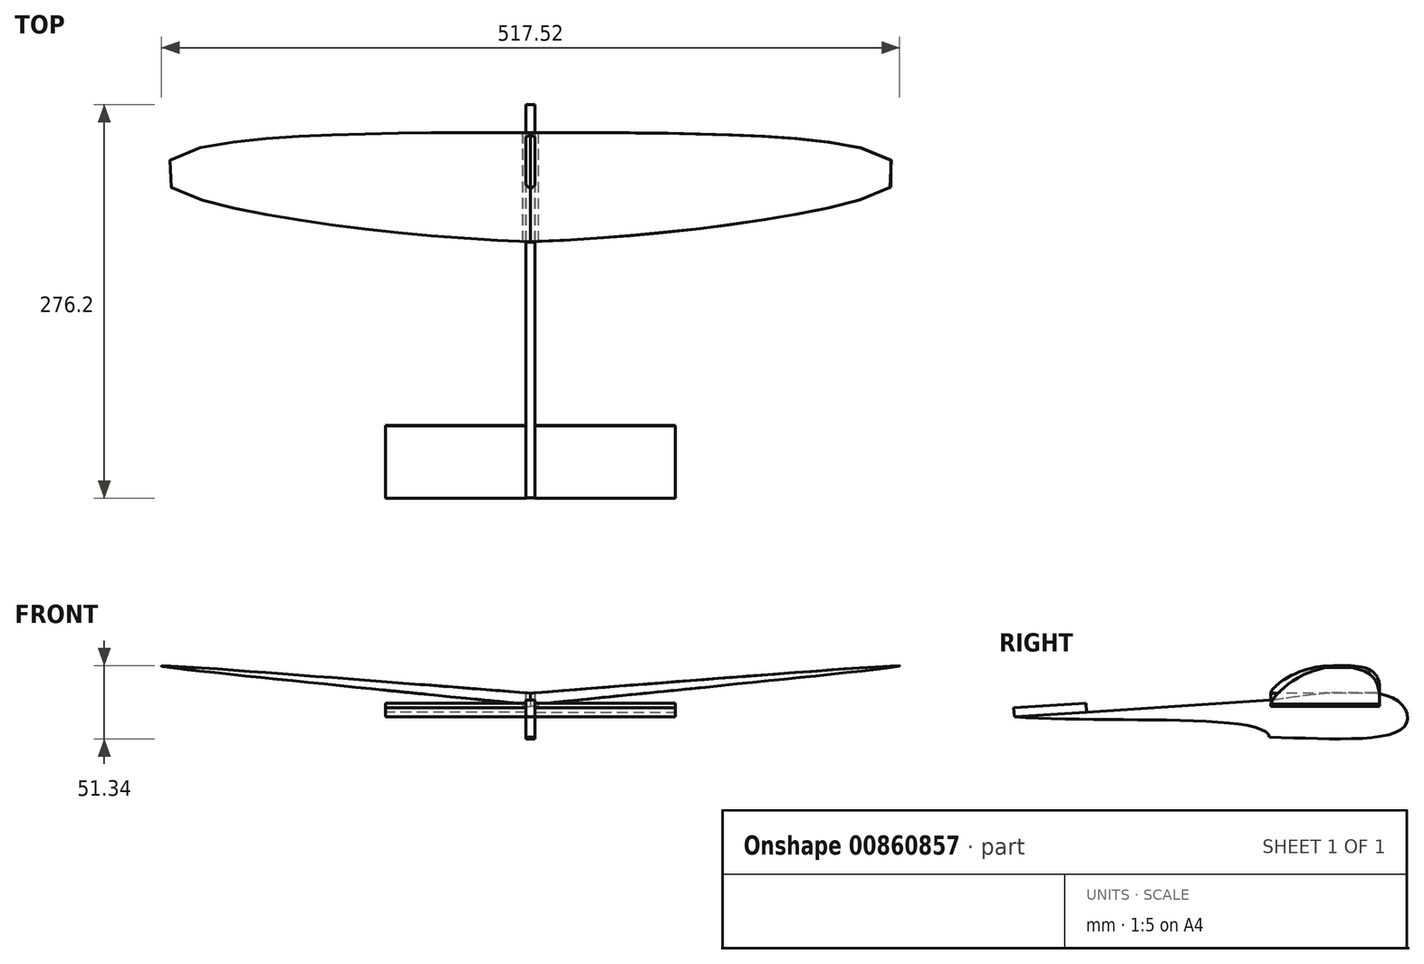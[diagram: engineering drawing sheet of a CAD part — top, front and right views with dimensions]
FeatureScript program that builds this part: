
annotation { "Feature Type Name" : "Feature", "Feature Type Description" : "" }
export const myFeature = defineFeature(function(context is Context, id is Id, definition is map)
    precondition{}
    {
        {
            var Q0;
            Q0=qCreatedBy(makeId("Top.planeOp"),FACE);
            cPlane(context, id + "F0", {"entities" : qUnion([Q0]), "cplaneType" : CPlaneType.OFFSET, "offset" : 21.59 * mm, "width" : 152.4 * mm, "height" : 152.4 * mm});
        }
        {
            var Q0;
            Q0=qCreatedBy(id+"F0.planeOp",FACE);
            var sketch = newSketch(context, id + "F1", { "sketchPlane" : qUnion([Q0])});
            skFitSpline(sketch, "E0", {"points": [v(0, 53.44) * mm, v(187.04, 49.14) * mm, v(254.61, 32.56) * mm, v(254, 16.59) * mm, v(0, -22.96) * mm], "startDerivative": vector(621.7, 0.16) * mm, "endDerivative": vector(-509.24, -9.47) * mm});
            skLineSegment(sketch, "E1", {"start": v(0, 0) * mm, "end": v(0, -100.13) * mm, "construction": true});
            skFitSpline(sketch, "E2.MirrorCS", {"points": [v(0, 53.44) * mm, v(-187.04, 49.14) * mm, v(-254.61, 32.56) * mm, v(-254, 16.59) * mm, v(0, -22.96) * mm], "startDerivative": vector(-621.7, 0.16) * mm, "endDerivative": vector(509.24, -9.47) * mm});
            skSolve(sketch);
        }
        {
            var Q0;
            Q0 = qSketchRegion(id + "F1", true);
            extrude(context, id + "F2", {"entities" : qUnion([Q0]), "depth" : 65.8 * mm, "offsetDistance" : 25.4 * mm});
        }
        {
            var Q0;
            Q0=qCreatedBy(makeId("Right.planeOp"),FACE);
            var sketch = newSketch(context, id + "F3", { "sketchPlane" : qUnion([Q0])});
            skLineSegment(sketch, "E3", {"start": v(-23.46, 26.13) * mm, "end": v(-23.7, 0) * mm});
            skLineSegment(sketch, "E4", {"start": v(-23.46, 26.13) * mm, "end": v(-202.7, 14.43) * mm});
            skFitSpline(sketch, "E5", {"points": [v(-202.7, 14.43) * mm, v(-23.7, 0) * mm], "startDerivative": vector(179.6, -14.43) * mm, "endDerivative": vector(3, -52.87) * mm});
            skFitSpline(sketch, "E6", {"points": [v(-23.46, 26.13) * mm, v(65.57, 26.13) * mm, v(70.56, 7.26) * mm, v(-23.7, 0) * mm], "startDerivative": vector(256.87, 37.76) * mm, "endDerivative": vector(-273.68, 3.75) * mm});
            skSolve(sketch);
        }
        {
            var Q0;
            Q0 = qSketchRegion(id + "F3", true);
            extrude(context, id + "F4", {"entities" : qUnion([Q0]), "endBound" : BoundingType.SYMMETRIC, "depth" : 6.35 * mm, "offsetDistance" : 25.4 * mm});
        }
        {
            var Q0;
            Q0=qCreatedBy(makeId("Front.planeOp"),FACE);
            var sketch = newSketch(context, id + "F5", { "sketchPlane" : qUnion([Q0])});
            skFitSpline(sketch, "E7", {"points": [v(-5.43, 23.45) * mm, v(-259.24, 50.17) * mm, v(0, 31) * mm], "startDerivative": vector(-765.3, 76.53) * mm, "endDerivative": vector(773.8, -61.22) * mm});
            skLineSegment(sketch, "E8", {"start": v(0, 31) * mm, "end": v(0, -86.9) * mm, "construction": true});
            skFitSpline(sketch, "E9.MirrorCS", {"points": [v(5.43, 23.45) * mm, v(259.24, 50.17) * mm, v(0, 31) * mm], "startDerivative": vector(765.3, 76.53) * mm, "endDerivative": vector(-773.8, -61.22) * mm});
            skLineSegment(sketch, "E10", {"start": v(5.43, 23.45) * mm, "end": v(5.43, 18.87) * mm});
            skLineSegment(sketch, "E11", {"start": v(-5.19, 18.87) * mm, "end": v(-5.43, 23.45) * mm});
            skLineSegment(sketch, "E12", {"start": v(266.18, 95.84) * mm, "end": v(-269, 95.84) * mm});
            skLineSegment(sketch, "E13", {"start": v(-265.64, 15.95) * mm, "end": v(-5.19, 18.87) * mm});
            skLineSegment(sketch, "E14", {"start": v(265.73, 14.57) * mm, "end": v(5.43, 18.87) * mm});
            skLineSegment(sketch, "E15", {"start": v(266.18, 95.84) * mm, "end": v(265.73, 14.57) * mm});
            skLineSegment(sketch, "E16", {"start": v(-269, 95.84) * mm, "end": v(-265.64, 15.95) * mm});
            skSolve(sketch);
        }
        {
            var Q0;
            Q0 = qSketchRegion(id + "F5", true);
            extrude(context, id + "F6", {"entities" : qUnion([Q0]), "operationType" : NewBodyOperationType.REMOVE, "endBound" : BoundingType.SYMMETRIC, "oppositeDirection" : true, "depth" : 127 * mm, "offsetDistance" : 25.4 * mm});
        }
        {
            var Q0;
            Q0=makeQuery(id+"F4.opExtrude","SWEPT_FACE",FACE,{"disambiguationData":[OSD([sQuery(id+"F3.wireOp",EDGE,"E4")])]});
            var sketch = newSketch(context, id + "F7", { "sketchPlane" : qUnion([Q0])});
            skPoint(sketch, "E17.0", {"position": v(0, -201.33) * mm});
            skLineSegment(sketch, "E18.bottom", {"start": v(0, -201.33) * mm, "end": v(-101.6, -201.33) * mm});
            skLineSegment(sketch, "E18.top", {"start": v(0, -150.53) * mm, "end": v(-101.6, -150.53) * mm});
            skLineSegment(sketch, "E18.left", {"start": v(0, -201.33) * mm, "end": v(0, -150.53) * mm});
            skLineSegment(sketch, "E18.right", {"start": v(-101.6, -201.33) * mm, "end": v(-101.6, -150.53) * mm});
            skLineSegment(sketch, "E19", {"start": v(0, -201.33) * mm, "end": v(0, -268.58) * mm, "construction": true});
            skLineSegment(sketch, "E20.MirrorCS", {"start": v(0, -201.33) * mm, "end": v(101.6, -201.33) * mm});
            skLineSegment(sketch, "E21.MirrorCS", {"start": v(0, -150.53) * mm, "end": v(101.6, -150.53) * mm});
            skLineSegment(sketch, "E22.MirrorCS", {"start": v(101.6, -201.33) * mm, "end": v(101.6, -150.53) * mm});
            skSolve(sketch);
        }
        {
            var Q0;
            {var subQ3=sQuery(id+"F7.wireOp",EDGE,"E22.MirrorCS");Q0=makeQuery(id+"F7.imprint","IMPRINT",FACE,{"disambiguationData":[TD([[makeQuery(id+"F7.imprint","IMPRINT",EDGE,{"derivedFrom":subQ3}),1.0]])]});}
            var Q1;
            {var subQ3=sQuery(id+"F7.wireOp",EDGE,"E18.right");Q1=makeQuery(id+"F7.imprint","IMPRINT",FACE,{"disambiguationData":[TD([[makeQuery(id+"F7.imprint","IMPRINT",EDGE,{"derivedFrom":subQ3}),-1.0]])]});}
            extrude(context, id + "F8", {"entities" : qUnion([Q0, Q1]), "depth" : 6.35 * mm, "offsetDistance" : 25.4 * mm});
        }
    });
